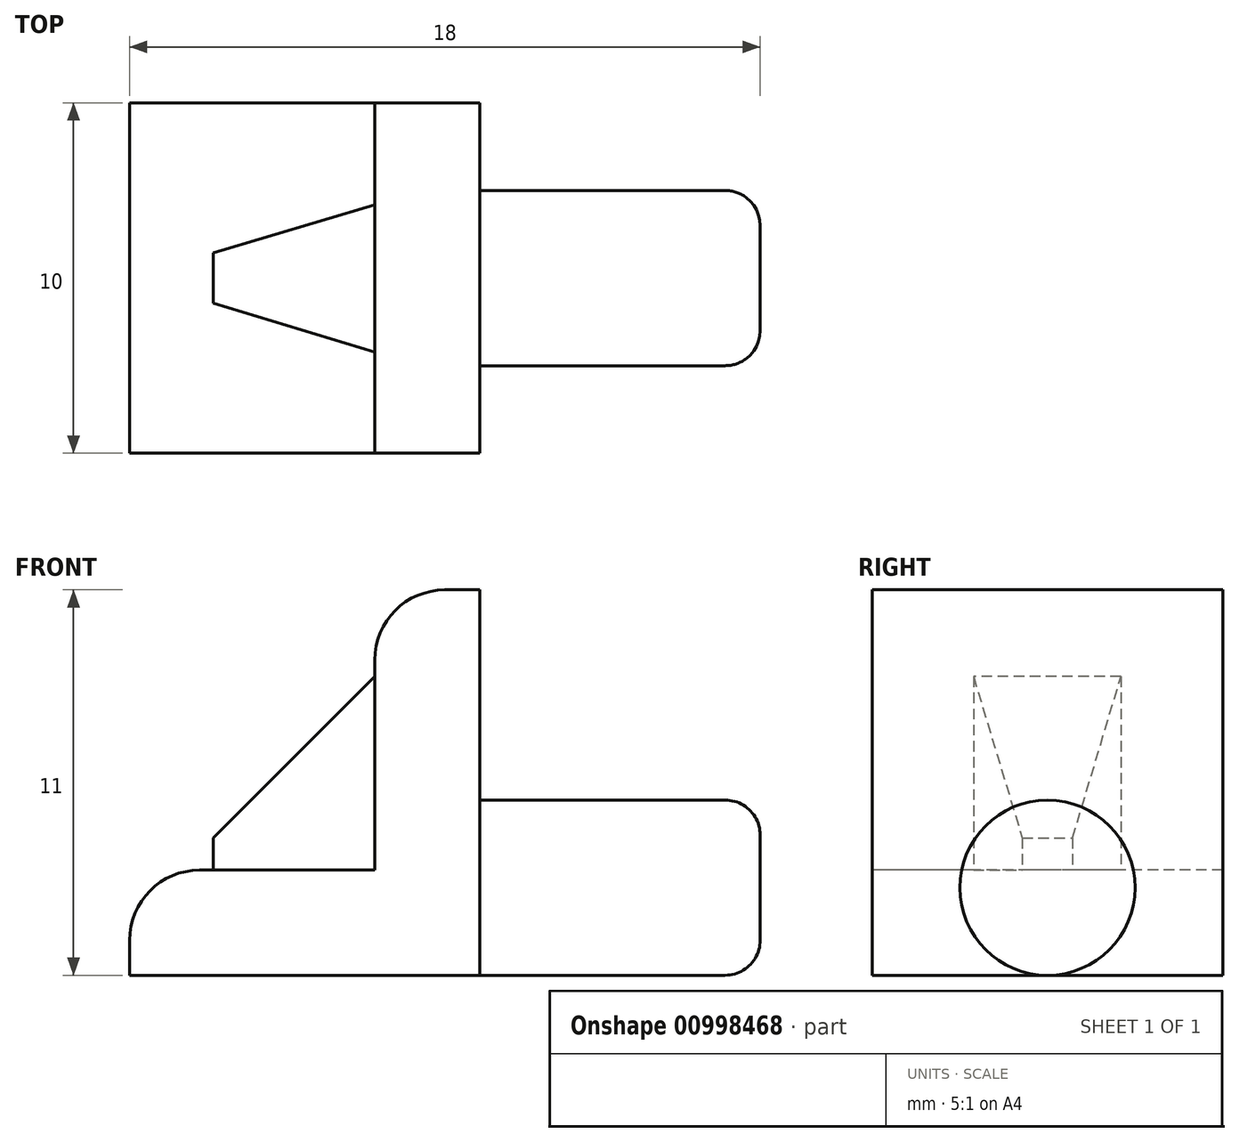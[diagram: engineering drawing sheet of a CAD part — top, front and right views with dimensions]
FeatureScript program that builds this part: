
annotation { "Feature Type Name" : "Feature", "Feature Type Description" : "" }
export const myFeature = defineFeature(function(context is Context, id is Id, definition is map)
    precondition{}
    {
        {
            var Q0;
            Q0=qCreatedBy(makeId("Top.planeOp"),FACE);
            var sketch = newSketch(context, id + "F0", { "sketchPlane" : qUnion([Q0])});
            skLineSegment(sketch, "E0.bottom", {"start": v(0, -2.95) * mm, "end": v(-10, -2.95) * mm});
            skLineSegment(sketch, "E0.top", {"start": v(0, -12.95) * mm, "end": v(-10, -12.95) * mm});
            skLineSegment(sketch, "E0.left", {"start": v(0, -2.95) * mm, "end": v(0, -12.95) * mm});
            skLineSegment(sketch, "E0.right", {"start": v(-10, -2.95) * mm, "end": v(-10, -12.95) * mm});
            skSolve(sketch);
        }
        {
            var Q0;
            Q0 = qSketchRegion(id + "F0", true);
            extrude(context, id + "F1", {"entities" : qUnion([Q0]), "depth" : 3 * mm, "offsetDistance" : 25.4 * mm});
        }
        {
            var Q0;
            Q0=makeQuery(id+"F1.opExtrude","CAP_FACE",FACE,{"disambiguationData":[OSD([sQuery(id+"F0.wireOp",EDGE,"E0.bottom"),sQuery(id+"F0.wireOp",EDGE,"E0.top"),sQuery(id+"F0.wireOp",EDGE,"E0.left"),sQuery(id+"F0.wireOp",EDGE,"E0.right")])],"isStart":false});
            var sketch = newSketch(context, id + "F2", { "sketchPlane" : qUnion([Q0])});
            skLineSegment(sketch, "E1.bottom", {"start": v(0, -2.95) * mm, "end": v(-3, -2.95) * mm});
            skLineSegment(sketch, "E1.top", {"start": v(0, -12.95) * mm, "end": v(-3, -12.95) * mm});
            skLineSegment(sketch, "E1.left", {"start": v(0, -2.95) * mm, "end": v(0, -12.95) * mm});
            skLineSegment(sketch, "E1.right", {"start": v(-3, -2.95) * mm, "end": v(-3, -12.95) * mm});
            skLineSegment(sketch, "E2", {"start": v(-3, -7.95) * mm, "end": v(-3, -5.85) * mm});
            skLineSegment(sketch, "E3", {"start": v(-3, -5.85) * mm, "end": v(-7.6, -7.23) * mm});
            skLineSegment(sketch, "E4", {"start": v(-3, -7.95) * mm, "end": v(-3, -10.06) * mm});
            skLineSegment(sketch, "E5", {"start": v(-3, -10.06) * mm, "end": v(-7.6, -8.67) * mm});
            skLineSegment(sketch, "E6", {"start": v(-7.6, -7.23) * mm, "end": v(-7.6, -8.67) * mm});
            skPoint(sketch, "E7.orphan", {"position": v(-10, -7.95) * mm});
            skSolve(sketch);
        }
        {
            var Q0;
            {var subQ1=sQuery(id+"F2.wireOp",EDGE,"E1.bottom");Q0=makeQuery(id+"F2.imprint","IMPRINT",FACE,{"disambiguationData":[TD([[makeQuery(id+"F2.imprint","IMPRINT",EDGE,{"derivedFrom":subQ1}),1.0]])]});}
            extrude(context, id + "F3", {"entities" : qUnion([Q0]), "operationType" : NewBodyOperationType.ADD, "depth" : 8 * mm, "offsetDistance" : 25.4 * mm});
        }
        {
            var Q0;
            {var subQ1=sQuery(id+"F2.wireOp",EDGE,"E3");Q0=makeQuery(id+"F2.imprint","IMPRINT",FACE,{"disambiguationData":[TD([[makeQuery(id+"F2.imprint","IMPRINT",EDGE,{"derivedFrom":subQ1}),1.0]])]});}
            extrude(context, id + "F4", {"entities" : qUnion([Q0]), "operationType" : NewBodyOperationType.ADD, "depth" : 6 * mm, "offsetDistance" : 25.4 * mm});
        }
        {
            var Q0;
            Q0=makeQuery(id+"F4.opExtrude","CAP_EDGE",EDGE,{"disambiguationData":[OSD([sQuery(id+"F2.wireOp",EDGE,"E6")])],"isStart":false});
            chamfer(context, id + "F5", {"entities" : qUnion([Q0]), "width" : 5.08 * mm, "tangentPropagation" : true});
        }
        {
            var Q0;
            Q0=makeQuery(id+"F1.opExtrude","CAP_EDGE",EDGE,{"disambiguationData":[OSD([sQuery(id+"F0.wireOp",EDGE,"E0.right")])],"isStart":false});
            var Q1;
            Q1=makeQuery(id+"F3.opExtrude","CAP_EDGE",EDGE,{"disambiguationData":[OSD([sQuery(id+"F2.wireOp",EDGE,"E1.right")])],"isStart":false});
            fillet(context, id + "F6", {"entities" : qUnion([Q0, Q1]), "radius" : 2 * mm, "tangentPropagation" : true, "allowEdgeOverflow" : false});
        }
        {
            var Q0;
            Q0=makeQuery(id+"F3.boolean.opBoolean","MERGE",FACE,{"derivedFrom":[makeQuery(id+"F1.opExtrude","SWEPT_FACE",FACE,{"disambiguationData":[OSD([sQuery(id+"F0.wireOp",EDGE,"E0.left")])]}),makeQuery(id+"F3.opExtrude","SWEPT_FACE",FACE,{"disambiguationData":[OSD([sQuery(id+"F2.wireOp",EDGE,"E1.left")])]})]});
            var sketch = newSketch(context, id + "F7", { "sketchPlane" : qUnion([Q0])});
            skCircle(sketch, "E8", {"center": v(-7.95, 2.5) * mm, "radius": 2.5 * mm});
            skPoint(sketch, "E9.orphan", {"position": v(-7.95, 5) * mm});
            skPoint(sketch, "E10.start.orphan", {"position": v(-7.95, 0) * mm});
            skSolve(sketch);
        }
        {
            var Q0;
            Q0=makeQuery(id+"F7.imprint","IMPRINT",FACE,{"disambiguationData":[TD([[makeQuery(id+"F7.imprint","IMPRINT",EDGE,{"derivedFrom":sQuery(id+"F7.wireOp",EDGE,"E8")}),1.0]])]});
            extrude(context, id + "F8", {"entities" : qUnion([Q0]), "operationType" : NewBodyOperationType.ADD, "depth" : 8 * mm, "offsetDistance" : 25.4 * mm});
        }
        {
            var Q0;
            Q0=makeQuery(id+"F8.opExtrude","CAP_EDGE",EDGE,{"disambiguationData":[OSD([sQuery(id+"F7.wireOp",EDGE,"E8")])],"isStart":false});
            fillet(context, id + "F9", {"entities" : qUnion([Q0]), "radius" : 1 * mm, "tangentPropagation" : true, "allowEdgeOverflow" : false});
        }
    });
